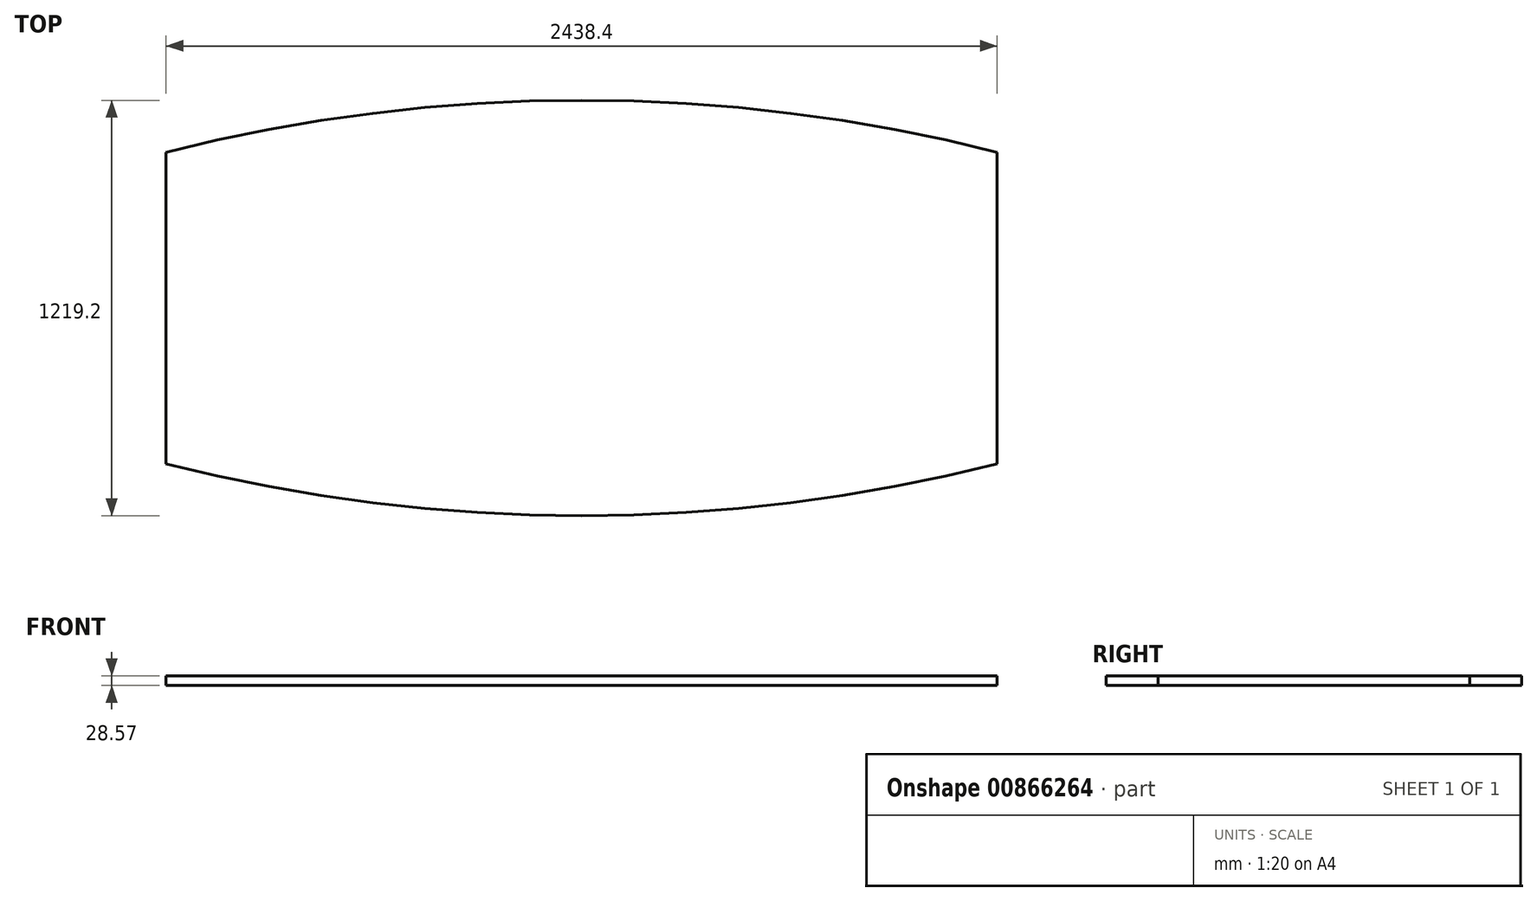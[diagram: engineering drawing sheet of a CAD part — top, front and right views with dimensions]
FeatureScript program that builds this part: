
annotation { "Feature Type Name" : "Feature", "Feature Type Description" : "" }
export const myFeature = defineFeature(function(context is Context, id is Id, definition is map)
    precondition{}
    {
        {
            var Q0;
            Q0=qCreatedBy(makeId("Top.planeOp"),FACE);
            var sketch = newSketch(context, id + "F0", { "sketchPlane" : qUnion([Q0])});
            skLineSegment(sketch, "E0.bottom", {"start": v(1219.2, 457.2) * mm, "end": v(-1219.2, 457.2) * mm});
            skLineSegment(sketch, "E0.top", {"start": v(1219.2, -457.2) * mm, "end": v(-1219.2, -457.2) * mm});
            skLineSegment(sketch, "E0.left", {"start": v(1219.2, 457.2) * mm, "end": v(1219.2, -457.2) * mm});
            skLineSegment(sketch, "E0.right", {"start": v(-1219.2, 457.2) * mm, "end": v(-1219.2, -457.2) * mm});
            skPoint(sketch, "E0.middle", {"position": v(0, 0) * mm});
            skLineSegment(sketch, "E1", {"start": v(0, 0) * mm, "end": v(0, 609.6) * mm});
            skPoint(sketch, "E1.endSnap0", {"position": v(0, 457.2) * mm});
            skLineSegment(sketch, "E2", {"start": v(0, 0) * mm, "end": v(0, -609.6) * mm});
            skPoint(sketch, "E2.endSnap0", {"position": v(0, -457.2) * mm});
            skArc(sketch, "E3", {"start": v(1219.2, 457.2) * mm, "mid": v(0, 609.6) * mm, "end": v(-1219.2, 457.2) * mm});
            skArc(sketch, "E4", {"start": v(-1219.2, -457.2) * mm, "mid": v(0, -609.6) * mm, "end": v(1219.2, -457.2) * mm});
            skSolve(sketch);
        }
        {
            var Q0;
            {var subQ0=sQuery(id+"F0.wireOp",EDGE,"E3");var subQ3=sQuery(id+"F0.wireOp",EDGE,"E1");var subQ5=makeQuery(id+"F0.imprint","INTERSECT",VERTEX,{"derivedFrom":[subQ3,subQ0]});Q0=makeQuery(id+"F0.imprint","IMPRINT",FACE,{"disambiguationData":[TD([[makeQuery(id+"F0.imprint","IMPRINT",EDGE,{"disambiguationData":[TD([[subQ5,1.0]])],"derivedFrom":subQ3}),1.0]])]});}
            var Q1;
            {var subQ0=sQuery(id+"F0.wireOp",EDGE,"E3");var subQ3=sQuery(id+"F0.wireOp",EDGE,"E1");var subQ5=makeQuery(id+"F0.imprint","INTERSECT",VERTEX,{"derivedFrom":[subQ3,subQ0]});Q1=makeQuery(id+"F0.imprint","IMPRINT",FACE,{"disambiguationData":[TD([[makeQuery(id+"F0.imprint","IMPRINT",EDGE,{"disambiguationData":[TD([[subQ5,1.0]])],"derivedFrom":subQ3}),-1.0]])]});}
            var Q2;
            {var subQ0=sQuery(id+"F0.wireOp",EDGE,"E0.right");Q2=makeQuery(id+"F0.imprint","IMPRINT",FACE,{"disambiguationData":[TD([[makeQuery(id+"F0.imprint","IMPRINT",EDGE,{"derivedFrom":subQ0}),1.0]])]});}
            var Q3;
            {var subQ5=sQuery(id+"F0.wireOp",EDGE,"E0.left");Q3=makeQuery(id+"F0.imprint","IMPRINT",FACE,{"disambiguationData":[TD([[makeQuery(id+"F0.imprint","IMPRINT",EDGE,{"derivedFrom":subQ5}),-1.0]])]});}
            var Q4;
            {var subQ0=sQuery(id+"F0.wireOp",EDGE,"E4");var subQ3=sQuery(id+"F0.wireOp",EDGE,"E2");var subQ5=makeQuery(id+"F0.imprint","INTERSECT",VERTEX,{"derivedFrom":[subQ3,subQ0]});Q4=makeQuery(id+"F0.imprint","IMPRINT",FACE,{"disambiguationData":[TD([[makeQuery(id+"F0.imprint","IMPRINT",EDGE,{"disambiguationData":[TD([[subQ5,1.0]])],"derivedFrom":subQ3}),-1.0]])]});}
            var Q5;
            {var subQ0=sQuery(id+"F0.wireOp",EDGE,"E4");var subQ3=sQuery(id+"F0.wireOp",EDGE,"E2");var subQ5=makeQuery(id+"F0.imprint","INTERSECT",VERTEX,{"derivedFrom":[subQ3,subQ0]});Q5=makeQuery(id+"F0.imprint","IMPRINT",FACE,{"disambiguationData":[TD([[makeQuery(id+"F0.imprint","IMPRINT",EDGE,{"disambiguationData":[TD([[subQ5,1.0]])],"derivedFrom":subQ3}),1.0]])]});}
            extrude(context, id + "F1", {"entities" : qUnion([Q0, Q1, Q2, Q3, Q4, Q5]), "depth" : 28.57 * mm, "offsetDistance" : 25.4 * mm});
        }
    });
